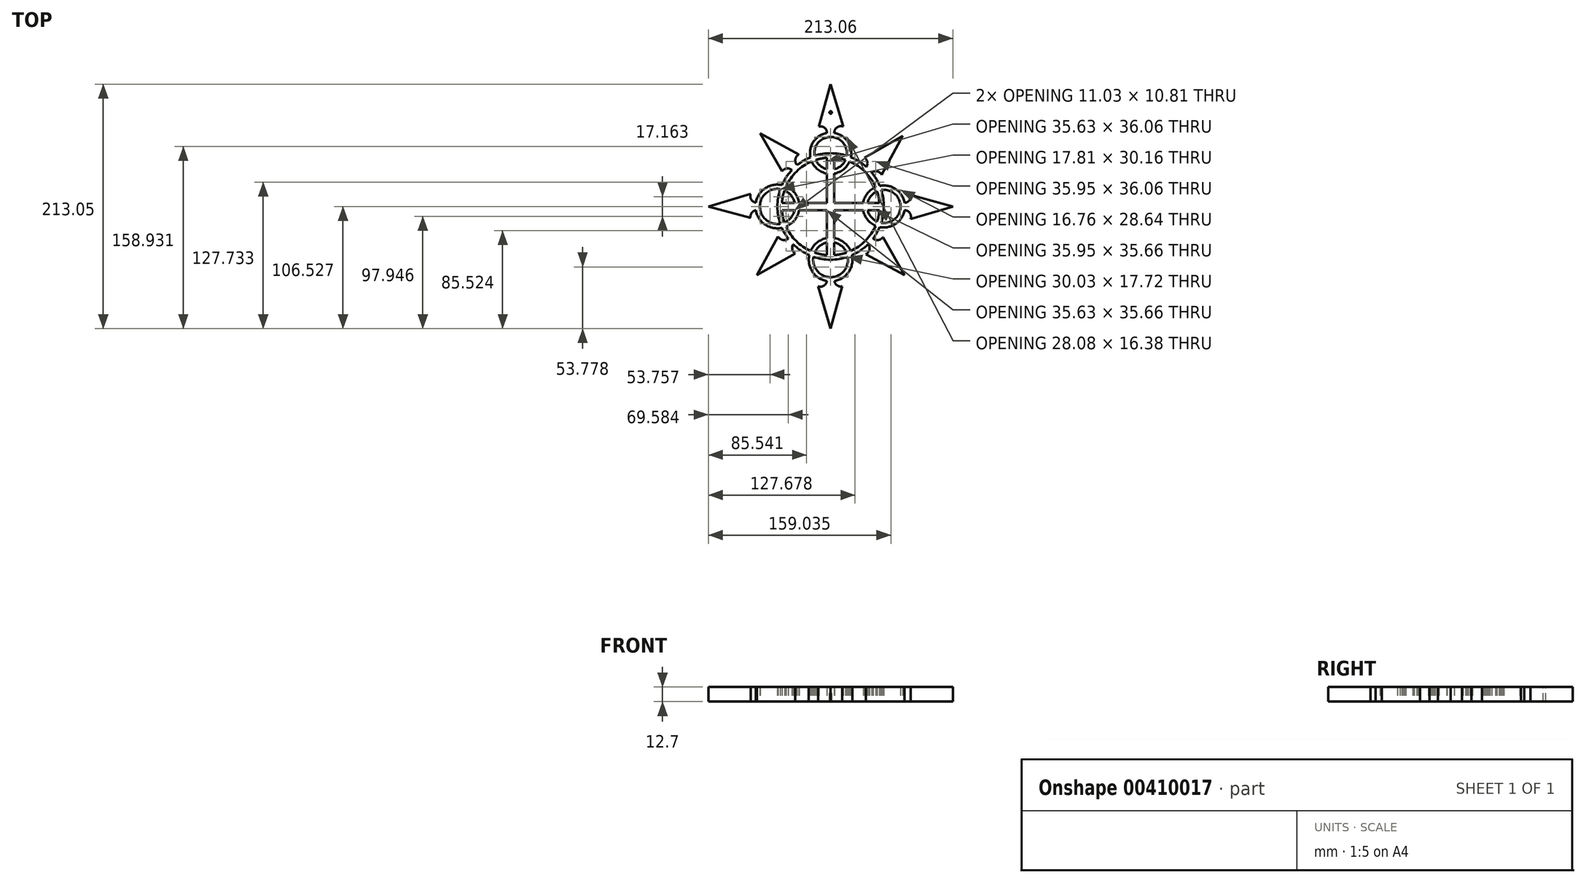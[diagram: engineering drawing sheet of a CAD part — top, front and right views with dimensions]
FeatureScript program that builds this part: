
annotation { "Feature Type Name" : "Feature", "Feature Type Description" : "" }
export const myFeature = defineFeature(function(context is Context, id is Id, definition is map)
    precondition{}
    {
        {
            var Q0;
            Q0=qCreatedBy(makeId("Top.planeOp"),FACE);
            var sketch = newSketch(context, id + "F0", { "sketchPlane" : qUnion([Q0])});
            skArc(sketch, "E0", {"start": v(14.04, 45.41) * mm, "mid": v(0, 47.59) * mm, "end": v(-14.04, 45.41) * mm});
            skArc(sketch, "E1", {"start": v(28.36, -1.98) * mm, "mid": v(32.02, -10.15) * mm, "end": v(39.12, -15.6) * mm});
            skArc(sketch, "E2", {"start": v(17.46, -37.63) * mm, "mid": v(11.74, -30.22) * mm, "end": v(3.18, -26.43) * mm});
            skArc(sketch, "E3", {"start": v(-27.55, 4.37) * mm, "mid": v(-31.35, 12.98) * mm, "end": v(-38.8, 18.73) * mm});
            skArc(sketch, "E4", {"start": v(17.67, 44.09) * mm, "mid": v(0, 65.6) * mm, "end": v(-17.67, 44.09) * mm});
            skArc(sketch, "E5.0", {"start": v(-3.17, 43.66) * mm, "mid": v(-8.12, 43) * mm, "end": v(-12.96, 41.76) * mm});
            skArc(sketch, "E6.0", {"start": v(14.04, 45.41) * mm, "mid": v(0, 61.8) * mm, "end": v(-14.04, 45.41) * mm});
            skArc(sketch, "E7.0", {"start": v(32.24, -1.98) * mm, "mid": v(35.17, -7.98) * mm, "end": v(40.47, -12.04) * mm});
            skArc(sketch, "E8.0", {"start": v(13.92, -39.04) * mm, "mid": v(9.6, -33.38) * mm, "end": v(3.18, -30.3) * mm});
            skArc(sketch, "E9.0", {"start": v(-31.43, 4.37) * mm, "mid": v(-34.52, 10.84) * mm, "end": v(-40.21, 15.19) * mm});
            skLineSegment(sketch, "E10.0", {"start": v(-3.17, 47.59) * mm, "end": v(-3.17, 47.48) * mm});
            skLineSegment(sketch, "E11.0", {"start": v(3.18, 47.59) * mm, "end": v(3.18, 47.48) * mm});
            skLineSegment(sketch, "E12.0", {"start": v(-46.39, -1.98) * mm, "end": v(-46.28, -1.98) * mm});
            skLineSegment(sketch, "E13.0", {"start": v(-46.39, 4.37) * mm, "end": v(-46.28, 4.37) * mm});
            skLineSegment(sketch, "E14.trimOffspring", {"start": v(-3.17, 43.66) * mm, "end": v(-3.17, 33.74) * mm});
            skLineSegment(sketch, "E15.trimOffspring", {"start": v(3.18, 43.66) * mm, "end": v(3.18, 33.74) * mm});
            skArc(sketch, "E16.trimOffspring", {"start": v(12.96, 41.76) * mm, "mid": v(8.12, 43) * mm, "end": v(3.18, 43.66) * mm});
            skArc(sketch, "E17.trimOffspring", {"start": v(-12.96, 41.76) * mm, "mid": v(-9, 36.6) * mm, "end": v(-3.17, 33.74) * mm});
            skArc(sketch, "E18.trimOffspring", {"start": v(-16.54, 40.43) * mm, "mid": v(-11.19, 33.46) * mm, "end": v(-3.17, 29.85) * mm});
            skArc(sketch, "E19.trimOffspring", {"start": v(-16.54, 40.43) * mm, "mid": v(-29.72, 31.69) * mm, "end": v(-38.8, 18.73) * mm});
            skArc(sketch, "E20.trimOffspring", {"start": v(3.18, 33.74) * mm, "mid": v(9, 36.6) * mm, "end": v(12.96, 41.76) * mm});
            skLineSegment(sketch, "E21.trimOffspring", {"start": v(-3.17, 29.85) * mm, "end": v(-3.17, 4.37) * mm});
            skLineSegment(sketch, "E22.trimOffspring", {"start": v(3.18, 29.85) * mm, "end": v(3.18, 4.37) * mm});
            skArc(sketch, "E23.trimOffspring", {"start": v(3.18, 29.85) * mm, "mid": v(11.19, 33.46) * mm, "end": v(16.54, 40.43) * mm});
            skArc(sketch, "E24.trimOffspring", {"start": v(-17.67, 44.09) * mm, "mid": v(-32.4, 34.39) * mm, "end": v(-42.46, 19.89) * mm});
            skLineSegment(sketch, "E25.trimOffspring", {"start": v(3.18, 4.37) * mm, "end": v(28.36, 4.37) * mm});
            skLineSegment(sketch, "E26.trimOffspring", {"start": v(3.18, -1.98) * mm, "end": v(3.18, -26.43) * mm});
            skLineSegment(sketch, "E27.trimOffspring", {"start": v(3.18, -1.98) * mm, "end": v(28.36, -1.98) * mm});
            skLineSegment(sketch, "E28.trimOffspring", {"start": v(-3.17, -1.98) * mm, "end": v(-3.17, -26.43) * mm});
            skLineSegment(sketch, "E29.trimOffspring", {"start": v(-27.55, 4.37) * mm, "end": v(-3.17, 4.37) * mm});
            skLineSegment(sketch, "E30.trimOffspring", {"start": v(-27.55, -1.98) * mm, "end": v(-3.17, -1.98) * mm});
            skArc(sketch, "E31.trimOffspring", {"start": v(-38.8, -16.33) * mm, "mid": v(-30.08, -28.94) * mm, "end": v(-17.46, -37.63) * mm});
            skArc(sketch, "E32.trimOffspring", {"start": v(-40.21, -12.8) * mm, "mid": v(-34.52, -8.44) * mm, "end": v(-31.43, -1.98) * mm});
            skArc(sketch, "E33.trimOffspring", {"start": v(-38.8, -16.33) * mm, "mid": v(-31.35, -10.58) * mm, "end": v(-27.55, -1.98) * mm});
            skArc(sketch, "E34.trimOffspring", {"start": v(-42.46, -17.5) * mm, "mid": v(-32.78, -31.63) * mm, "end": v(-18.62, -41.29) * mm});
            skArc(sketch, "E35.trimOffspring", {"start": v(-42.46, -1.98) * mm, "mid": v(-41.69, -7.46) * mm, "end": v(-40.21, -12.8) * mm});
            skLineSegment(sketch, "E36.trimOffspring", {"start": v(-42.46, 4.37) * mm, "end": v(-31.43, 4.37) * mm});
            skLineSegment(sketch, "E37.trimOffspring", {"start": v(-42.46, -1.98) * mm, "end": v(-31.43, -1.98) * mm});
            skArc(sketch, "E38.trimOffspring", {"start": v(-40.21, 15.19) * mm, "mid": v(-41.69, 9.85) * mm, "end": v(-42.46, 4.37) * mm});
            skArc(sketch, "E39.trimOffspring", {"start": v(-42.46, 19.89) * mm, "mid": v(-65.49, 1.2) * mm, "end": v(-42.46, -17.5) * mm});
            skArc(sketch, "E40.trimOffspring", {"start": v(-43.87, 16.28) * mm, "mid": v(-61.68, 1.2) * mm, "end": v(-43.87, -13.88) * mm});
            skArc(sketch, "E41.trimOffspring", {"start": v(-43.87, 16.28) * mm, "mid": v(-46.39, 1.2) * mm, "end": v(-43.87, -13.88) * mm});
            skLineSegment(sketch, "E42.trimOffspring", {"start": v(32.24, 4.37) * mm, "end": v(42.46, 4.37) * mm});
            skLineSegment(sketch, "E43.trimOffspring", {"start": v(32.24, -1.98) * mm, "end": v(42.46, -1.98) * mm});
            skArc(sketch, "E44.trimOffspring", {"start": v(42.46, 4.37) * mm, "mid": v(41.77, 9.46) * mm, "end": v(40.47, 14.43) * mm});
            skLineSegment(sketch, "E45.trimOffspring", {"start": v(46.28, 4.37) * mm, "end": v(46.39, 4.37) * mm});
            skLineSegment(sketch, "E46.trimOffspring", {"start": v(46.28, -1.98) * mm, "end": v(46.39, -1.98) * mm});
            skArc(sketch, "E47.trimOffspring", {"start": v(40.47, 14.43) * mm, "mid": v(35.17, 10.38) * mm, "end": v(32.24, 4.37) * mm});
            skArc(sketch, "E48.trimOffspring", {"start": v(39.12, 18) * mm, "mid": v(30, 31.4) * mm, "end": v(16.54, 40.43) * mm});
            skArc(sketch, "E49.trimOffspring", {"start": v(39.12, 18) * mm, "mid": v(32.02, 12.54) * mm, "end": v(28.36, 4.37) * mm});
            skArc(sketch, "E50.trimOffspring", {"start": v(42.78, 19.15) * mm, "mid": v(32.7, 34.1) * mm, "end": v(17.67, 44.09) * mm});
            skArc(sketch, "E51.trimOffspring", {"start": v(44.12, -13.12) * mm, "mid": v(60.89, 1.2) * mm, "end": v(44.12, 15.52) * mm});
            skArc(sketch, "E52.trimOffspring", {"start": v(42.78, -16.75) * mm, "mid": v(64.7, 1.2) * mm, "end": v(42.78, 19.15) * mm});
            skArc(sketch, "E53.trimOffspring", {"start": v(40.47, -12.04) * mm, "mid": v(41.77, -7.07) * mm, "end": v(42.46, -1.98) * mm});
            skArc(sketch, "E54.trimOffspring", {"start": v(44.12, -13.12) * mm, "mid": v(46.39, 1.2) * mm, "end": v(44.12, 15.52) * mm});
            skArc(sketch, "E55.trimOffspring", {"start": v(17.46, -37.63) * mm, "mid": v(30.36, -28.65) * mm, "end": v(39.12, -15.6) * mm});
            skArc(sketch, "E56.trimOffspring", {"start": v(18.62, -41.29) * mm, "mid": v(33.06, -31.34) * mm, "end": v(42.78, -16.75) * mm});
            skLineSegment(sketch, "E57.trimOffspring", {"start": v(3.18, -45.08) * mm, "end": v(3.18, -45.2) * mm});
            skArc(sketch, "E58.trimOffspring", {"start": v(3.18, -41.26) * mm, "mid": v(8.62, -40.5) * mm, "end": v(13.92, -39.04) * mm});
            skLineSegment(sketch, "E59.trimOffspring", {"start": v(-3.17, -45.08) * mm, "end": v(-3.17, -45.2) * mm});
            skArc(sketch, "E60.trimOffspring", {"start": v(-13.92, -39.04) * mm, "mid": v(-8.62, -40.5) * mm, "end": v(-3.17, -41.26) * mm});
            skArc(sketch, "E61.trimOffspring", {"start": v(-15.01, -42.7) * mm, "mid": v(0, -60.4) * mm, "end": v(15.01, -42.7) * mm});
            skArc(sketch, "E62.trimOffspring", {"start": v(-15.01, -42.7) * mm, "mid": v(0, -45.2) * mm, "end": v(15.01, -42.7) * mm});
            skArc(sketch, "E63.trimOffspring", {"start": v(-18.62, -41.29) * mm, "mid": v(0, -64.22) * mm, "end": v(18.62, -41.29) * mm});
            skArc(sketch, "E64", {"start": v(-3.17, 65.32) * mm, "mid": v(-5.3, 69.78) * mm, "end": v(-10.12, 70.92) * mm});
            skArc(sketch, "E65", {"start": v(10.92, 70.92) * mm, "mid": v(5.62, 70.1) * mm, "end": v(3.18, 65.32) * mm});
            skLineSegment(sketch, "E66", {"start": v(-10.12, 70.92) * mm, "end": v(0, 107.72) * mm});
            skLineSegment(sketch, "E67", {"start": v(0, 107.72) * mm, "end": v(10.92, 70.92) * mm});
            skLineSegment(sketch, "E68.1.0", {"start": v(-42.46, 31.71) * mm, "end": v(-61.32, 64.89) * mm});
            skLineSegment(sketch, "E68.1.1", {"start": v(-61.32, 64.89) * mm, "end": v(-27.58, 46.6) * mm});
            skArc(sketch, "E68.1.2", {"start": v(-27.58, 46.6) * mm, "mid": v(-30.75, 42.26) * mm, "end": v(-29.1, 37.15) * mm});
            skArc(sketch, "E68.1.3", {"start": v(-33.58, 32.66) * mm, "mid": v(-38.25, 34.3) * mm, "end": v(-42.46, 31.71) * mm});
            skLineSegment(sketch, "E68.2.0", {"start": v(-69.73, -8.92) * mm, "end": v(-106.53, 1.2) * mm});
            skLineSegment(sketch, "E68.2.1", {"start": v(-106.53, 1.2) * mm, "end": v(-69.73, 12.12) * mm});
            skArc(sketch, "E68.2.2", {"start": v(-69.73, 12.12) * mm, "mid": v(-68.9, 6.82) * mm, "end": v(-64.12, 4.37) * mm});
            skArc(sketch, "E68.2.3", {"start": v(-64.12, -1.98) * mm, "mid": v(-68.58, -4.1) * mm, "end": v(-69.73, -8.92) * mm});
            skLineSegment(sketch, "E68.3.0", {"start": v(-30.95, -39.81) * mm, "end": v(-64.12, -58.68) * mm});
            skLineSegment(sketch, "E68.3.1", {"start": v(-64.12, -58.68) * mm, "end": v(-45.83, -24.93) * mm});
            skArc(sketch, "E68.3.2", {"start": v(-45.83, -24.93) * mm, "mid": v(-41.5, -28.1) * mm, "end": v(-36.38, -26.45) * mm});
            skArc(sketch, "E68.3.3", {"start": v(-31.9, -30.94) * mm, "mid": v(-33.54, -35.6) * mm, "end": v(-30.95, -39.81) * mm});
            skLineSegment(sketch, "E68.4.0", {"start": v(10.12, -68.53) * mm, "end": v(0, -105.33) * mm});
            skLineSegment(sketch, "E68.4.1", {"start": v(0, -105.33) * mm, "end": v(-10.92, -68.53) * mm});
            skArc(sketch, "E68.4.2", {"start": v(-10.92, -68.53) * mm, "mid": v(-5.62, -67.7) * mm, "end": v(-3.17, -62.93) * mm});
            skArc(sketch, "E68.4.3", {"start": v(3.18, -62.93) * mm, "mid": v(5.3, -67.39) * mm, "end": v(10.12, -68.53) * mm});
            skLineSegment(sketch, "E68.5.0", {"start": v(45.6, -25.5) * mm, "end": v(64.47, -58.68) * mm});
            skLineSegment(sketch, "E68.5.1", {"start": v(64.47, -58.68) * mm, "end": v(30.72, -40.38) * mm});
            skArc(sketch, "E68.5.2", {"start": v(30.72, -40.38) * mm, "mid": v(33.89, -36.05) * mm, "end": v(32.24, -30.94) * mm});
            skArc(sketch, "E68.5.3", {"start": v(36.73, -26.45) * mm, "mid": v(41.39, -28.1) * mm, "end": v(45.6, -25.5) * mm});
            skLineSegment(sketch, "E68.6.0", {"start": v(69.73, 11.32) * mm, "end": v(106.53, 1.2) * mm});
            skLineSegment(sketch, "E68.6.1", {"start": v(106.53, 1.2) * mm, "end": v(69.73, -9.73) * mm});
            skArc(sketch, "E68.6.2", {"start": v(69.73, -9.73) * mm, "mid": v(68.9, -4.42) * mm, "end": v(64.12, -1.98) * mm});
            skArc(sketch, "E68.6.3", {"start": v(64.12, 4.37) * mm, "mid": v(68.58, 6.5) * mm, "end": v(69.73, 11.32) * mm});
            skLineSegment(sketch, "E68.7.0", {"start": v(29.51, 43.66) * mm, "end": v(62.69, 62.53) * mm});
            skLineSegment(sketch, "E68.7.1", {"start": v(62.69, 62.53) * mm, "end": v(44.4, 28.78) * mm});
            skArc(sketch, "E68.7.2", {"start": v(44.4, 28.78) * mm, "mid": v(40.06, 31.95) * mm, "end": v(34.95, 30.3) * mm});
            skArc(sketch, "E68.7.3", {"start": v(30.46, 34.79) * mm, "mid": v(32.1, 39.45) * mm, "end": v(29.51, 43.66) * mm});
            skArc(sketch, "E69.trimOffspring", {"start": v(-3.17, -30.3) * mm, "mid": v(-9.6, -33.38) * mm, "end": v(-13.92, -39.04) * mm});
            skLineSegment(sketch, "E70.trimOffspring", {"start": v(3.18, -30.3) * mm, "end": v(3.18, -41.26) * mm});
            skArc(sketch, "E71.trimOffspring", {"start": v(-3.17, -26.43) * mm, "mid": v(-11.74, -30.22) * mm, "end": v(-17.46, -37.63) * mm});
            skLineSegment(sketch, "E72.trimOffspring", {"start": v(-3.17, -30.3) * mm, "end": v(-3.17, -41.26) * mm});
            skPoint(sketch, "E73", {"position": v(0, 84.81) * mm});
            skSolve(sketch);
        }
        {
            var Q0;
            Q0=qSketchRegion(id+"F0",true);
            extrude(context, id + "F1", {"entities" : qUnion([Q0]), "depth" : 12.7 * mm});
        }
        {
            var Q0;
            Q0=qCreatedBy(makeId("Top.planeOp"),FACE);
            cPlane(context, id + "F2", {"entities" : qUnion([Q0]), "cplaneType" : CPlaneType.OFFSET, "offset" : 12.95 * mm, "width" : 152.4 * mm, "height" : 152.4 * mm});
        }
        {
            var Q0;
            Q0=qCreatedBy(id+"F2.planeOp",FACE);
            var sketch = newSketch(context, id + "F3", { "sketchPlane" : qUnion([Q0])});
            skPoint(sketch, "E74", {"position": v(0, 83.14) * mm});
            skSolve(sketch);
        }
        {
            var Q0;
            Q0=sQuery(id+"F3.wireOp",VERTEX,"E74");
            var Q1;
            Q1=makeQuery(id+"F1.opExtrude","SWEPT_BODY",BODY,{"disambiguationData":[OSD([sQuery(id+"F0.wireOp",EDGE,"E0"),sQuery(id+"F0.wireOp",EDGE,"E1"),sQuery(id+"F0.wireOp",EDGE,"E2"),sQuery(id+"F0.wireOp",EDGE,"E3"),sQuery(id+"F0.wireOp",EDGE,"E4"),sQuery(id+"F0.wireOp",EDGE,"E5.0"),sQuery(id+"F0.wireOp",EDGE,"E6.0"),sQuery(id+"F0.wireOp",EDGE,"E7.0"),sQuery(id+"F0.wireOp",EDGE,"E8.0"),sQuery(id+"F0.wireOp",EDGE,"E9.0"),sQuery(id+"F0.wireOp",EDGE,"E14.trimOffspring"),sQuery(id+"F0.wireOp",EDGE,"E15.trimOffspring"),sQuery(id+"F0.wireOp",EDGE,"E16.trimOffspring"),sQuery(id+"F0.wireOp",EDGE,"E17.trimOffspring"),sQuery(id+"F0.wireOp",EDGE,"E18.trimOffspring"),sQuery(id+"F0.wireOp",EDGE,"E19.trimOffspring"),sQuery(id+"F0.wireOp",EDGE,"E20.trimOffspring"),sQuery(id+"F0.wireOp",EDGE,"E21.trimOffspring"),sQuery(id+"F0.wireOp",EDGE,"E22.trimOffspring"),sQuery(id+"F0.wireOp",EDGE,"E23.trimOffspring"),sQuery(id+"F0.wireOp",EDGE,"E24.trimOffspring"),sQuery(id+"F0.wireOp",EDGE,"E25.trimOffspring"),sQuery(id+"F0.wireOp",EDGE,"E26.trimOffspring"),sQuery(id+"F0.wireOp",EDGE,"E27.trimOffspring"),sQuery(id+"F0.wireOp",EDGE,"E28.trimOffspring"),sQuery(id+"F0.wireOp",EDGE,"E29.trimOffspring"),sQuery(id+"F0.wireOp",EDGE,"E30.trimOffspring"),sQuery(id+"F0.wireOp",EDGE,"E31.trimOffspring"),sQuery(id+"F0.wireOp",EDGE,"E32.trimOffspring"),sQuery(id+"F0.wireOp",EDGE,"E33.trimOffspring"),sQuery(id+"F0.wireOp",EDGE,"E34.trimOffspring"),sQuery(id+"F0.wireOp",EDGE,"E35.trimOffspring"),sQuery(id+"F0.wireOp",EDGE,"E36.trimOffspring"),sQuery(id+"F0.wireOp",EDGE,"E37.trimOffspring"),sQuery(id+"F0.wireOp",EDGE,"E38.trimOffspring"),sQuery(id+"F0.wireOp",EDGE,"E39.trimOffspring"),sQuery(id+"F0.wireOp",EDGE,"E40.trimOffspring"),sQuery(id+"F0.wireOp",EDGE,"E41.trimOffspring"),sQuery(id+"F0.wireOp",EDGE,"E42.trimOffspring"),sQuery(id+"F0.wireOp",EDGE,"E43.trimOffspring"),sQuery(id+"F0.wireOp",EDGE,"E44.trimOffspring"),sQuery(id+"F0.wireOp",EDGE,"E47.trimOffspring"),sQuery(id+"F0.wireOp",EDGE,"E48.trimOffspring"),sQuery(id+"F0.wireOp",EDGE,"E49.trimOffspring"),sQuery(id+"F0.wireOp",EDGE,"E50.trimOffspring"),sQuery(id+"F0.wireOp",EDGE,"E51.trimOffspring"),sQuery(id+"F0.wireOp",EDGE,"E52.trimOffspring"),sQuery(id+"F0.wireOp",EDGE,"E53.trimOffspring"),sQuery(id+"F0.wireOp",EDGE,"E54.trimOffspring"),sQuery(id+"F0.wireOp",EDGE,"E55.trimOffspring"),sQuery(id+"F0.wireOp",EDGE,"E56.trimOffspring"),sQuery(id+"F0.wireOp",EDGE,"E58.trimOffspring"),sQuery(id+"F0.wireOp",EDGE,"E60.trimOffspring"),sQuery(id+"F0.wireOp",EDGE,"E61.trimOffspring"),sQuery(id+"F0.wireOp",EDGE,"E62.trimOffspring"),sQuery(id+"F0.wireOp",EDGE,"E63.trimOffspring"),sQuery(id+"F0.wireOp",EDGE,"E64"),sQuery(id+"F0.wireOp",EDGE,"E65"),sQuery(id+"F0.wireOp",EDGE,"E66"),sQuery(id+"F0.wireOp",EDGE,"E67"),sQuery(id+"F0.wireOp",EDGE,"E68.1.0"),sQuery(id+"F0.wireOp",EDGE,"E68.1.1"),sQuery(id+"F0.wireOp",EDGE,"E68.1.2"),sQuery(id+"F0.wireOp",EDGE,"E68.1.3"),sQuery(id+"F0.wireOp",EDGE,"E68.2.0"),sQuery(id+"F0.wireOp",EDGE,"E68.2.1"),sQuery(id+"F0.wireOp",EDGE,"E68.2.2"),sQuery(id+"F0.wireOp",EDGE,"E68.2.3"),sQuery(id+"F0.wireOp",EDGE,"E68.3.0"),sQuery(id+"F0.wireOp",EDGE,"E68.3.1"),sQuery(id+"F0.wireOp",EDGE,"E68.3.2"),sQuery(id+"F0.wireOp",EDGE,"E68.3.3"),sQuery(id+"F0.wireOp",EDGE,"E68.4.0"),sQuery(id+"F0.wireOp",EDGE,"E68.4.1"),sQuery(id+"F0.wireOp",EDGE,"E68.4.2"),sQuery(id+"F0.wireOp",EDGE,"E68.4.3"),sQuery(id+"F0.wireOp",EDGE,"E68.5.0"),sQuery(id+"F0.wireOp",EDGE,"E68.5.1"),sQuery(id+"F0.wireOp",EDGE,"E68.5.2"),sQuery(id+"F0.wireOp",EDGE,"E68.5.3"),sQuery(id+"F0.wireOp",EDGE,"E68.6.0"),sQuery(id+"F0.wireOp",EDGE,"E68.6.1"),sQuery(id+"F0.wireOp",EDGE,"E68.6.2"),sQuery(id+"F0.wireOp",EDGE,"E68.6.3"),sQuery(id+"F0.wireOp",EDGE,"E68.7.0"),sQuery(id+"F0.wireOp",EDGE,"E68.7.1"),sQuery(id+"F0.wireOp",EDGE,"E68.7.2"),sQuery(id+"F0.wireOp",EDGE,"E68.7.3"),sQuery(id+"F0.wireOp",EDGE,"E69.trimOffspring"),sQuery(id+"F0.wireOp",EDGE,"E70.trimOffspring"),sQuery(id+"F0.wireOp",EDGE,"E71.trimOffspring"),sQuery(id+"F0.wireOp",EDGE,"E72.trimOffspring")])]});
            hole(context, id + "F4", {"style" : HoleStyle.SIMPLE, "endStyle" : HoleEndStyle.BLIND, "holeDiameter" : 2.08 * mm, "holeDepth" : 50.8 * mm, "tappedDepth" : 12.7 * mm, "tapClearance" : 3, "startFromSketch" : true, "locations" : qUnion([Q0]), "scope" : qUnion([Q1])});
        }
    });
